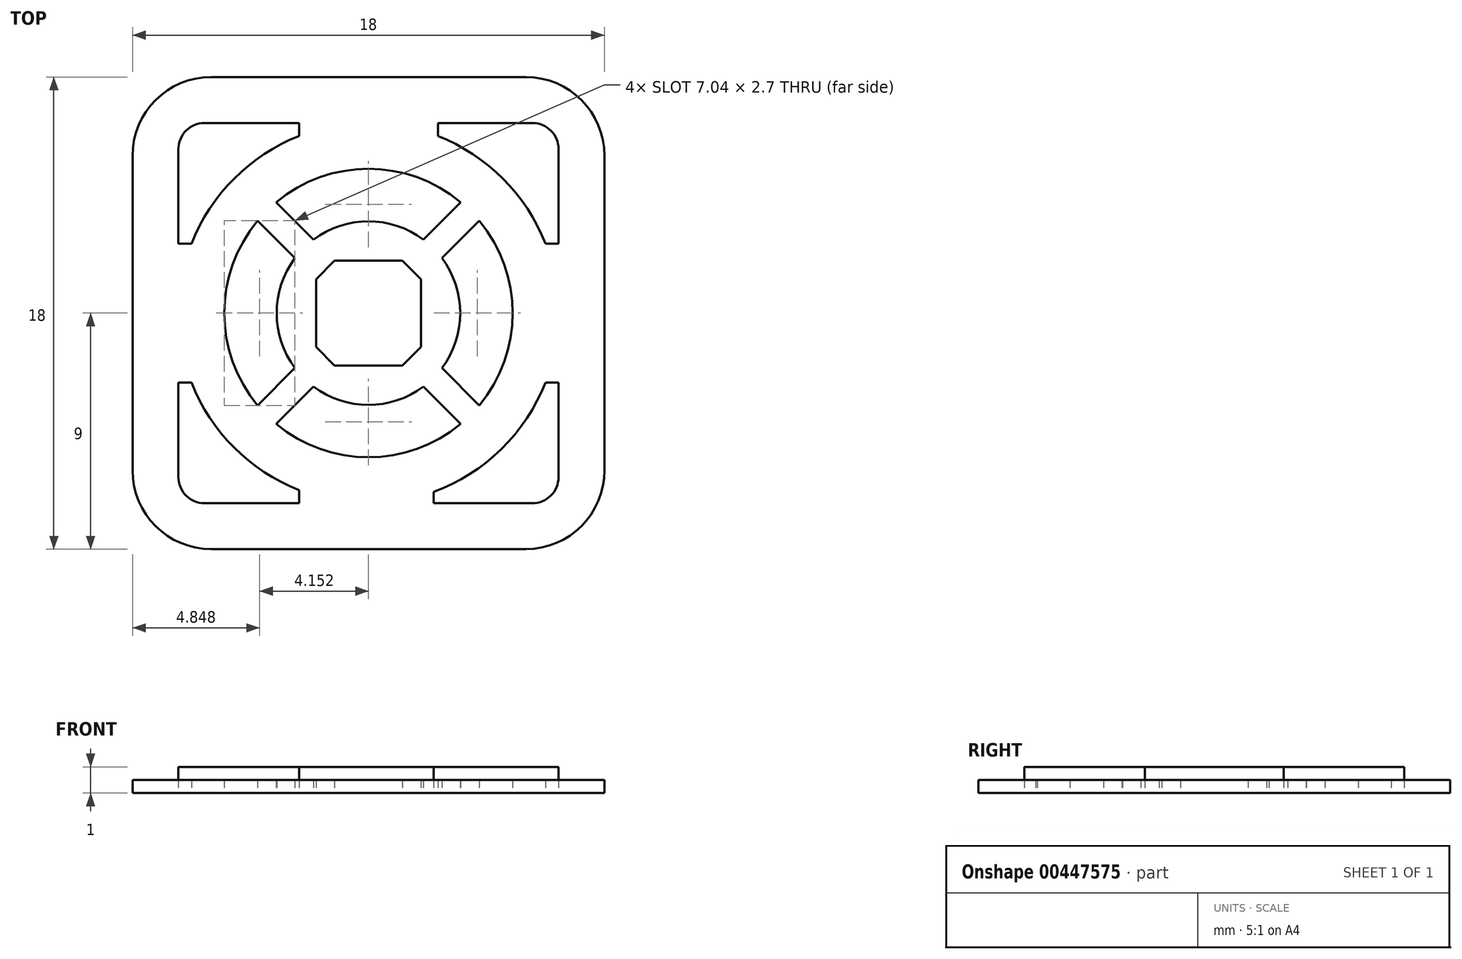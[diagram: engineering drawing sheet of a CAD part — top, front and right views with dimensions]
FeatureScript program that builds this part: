
annotation { "Feature Type Name" : "Feature", "Feature Type Description" : "" }
export const myFeature = defineFeature(function(context is Context, id is Id, definition is map)
    precondition{}
    {
        {
            var Q0;
            Q0=qCreatedBy(makeId("Top.planeOp"),FACE);
            var sketch = newSketch(context, id + "F0", { "sketchPlane" : qUnion([Q0])});
            skLineSegment(sketch, "E0.bottom", {"start": v(6, -9) * mm, "end": v(-6, -9) * mm});
            skLineSegment(sketch, "E0.top", {"start": v(6, 9) * mm, "end": v(-6, 9) * mm});
            skLineSegment(sketch, "E0.left", {"start": v(9, -6) * mm, "end": v(9, 6) * mm});
            skLineSegment(sketch, "E0.right", {"start": v(-9, -6) * mm, "end": v(-9, 6) * mm});
            skPoint(sketch, "E0.middle", {"position": v(0, 0) * mm});
            skLineSegment(sketch, "E1.bottom", {"start": v(1.3, -2) * mm, "end": v(-1.3, -2) * mm});
            skLineSegment(sketch, "E1.top", {"start": v(1.3, 2) * mm, "end": v(-1.3, 2) * mm});
            skLineSegment(sketch, "E1.left", {"start": v(2, -1.3) * mm, "end": v(2, 1.3) * mm});
            skLineSegment(sketch, "E1.right", {"start": v(-2, -1.3) * mm, "end": v(-2, 1.3) * mm});
            skLineSegment(sketch, "E2", {"start": v(-2, 1.3) * mm, "end": v(-1.3, 2) * mm});
            skLineSegment(sketch, "E3", {"start": v(1.3, 2) * mm, "end": v(2, 1.3) * mm});
            skLineSegment(sketch, "E4", {"start": v(-2, -1.3) * mm, "end": v(-1.3, -2) * mm});
            skLineSegment(sketch, "E5", {"start": v(1.3, -2) * mm, "end": v(2, -1.3) * mm});
            skPoint(sketch, "E6.orphan", {"position": v(-2, 2) * mm});
            skPoint(sketch, "E7.orphan", {"position": v(2, 2) * mm});
            skPoint(sketch, "E8.orphan", {"position": v(2, -2) * mm});
            skPoint(sketch, "E9.orphan", {"position": v(-2, -2) * mm});
            skArc(sketch, "E10", {"start": v(-2.8, 2.1) * mm, "mid": v(-3.5, 0) * mm, "end": v(-2.8, -2.1) * mm});
            skArc(sketch, "E11", {"start": v(-4.23, 3.52) * mm, "mid": v(-5.5, 0) * mm, "end": v(-4.23, -3.52) * mm});
            skLineSegment(sketch, "E12", {"start": v(-9, 9) * mm, "end": v(9, -9) * mm, "construction": true});
            skLineSegment(sketch, "E13", {"start": v(9, 9) * mm, "end": v(-9, -9) * mm, "construction": true});
            skLineSegment(sketch, "E14", {"start": v(-4.23, 3.52) * mm, "end": v(-2.8, 2.1) * mm});
            skLineSegment(sketch, "E15", {"start": v(-2.1, 2.8) * mm, "end": v(-3.52, 4.23) * mm});
            skLineSegment(sketch, "E16", {"start": v(2.1, 2.8) * mm, "end": v(3.52, 4.23) * mm});
            skLineSegment(sketch, "E17", {"start": v(2.8, 2.1) * mm, "end": v(4.23, 3.52) * mm});
            skLineSegment(sketch, "E18", {"start": v(-3.52, -4.23) * mm, "end": v(-2.1, -2.8) * mm});
            skLineSegment(sketch, "E19", {"start": v(-4.23, -3.52) * mm, "end": v(-2.8, -2.1) * mm});
            skLineSegment(sketch, "E20", {"start": v(2.1, -2.8) * mm, "end": v(3.52, -4.23) * mm});
            skLineSegment(sketch, "E21", {"start": v(2.8, -2.1) * mm, "end": v(4.23, -3.52) * mm});
            skArc(sketch, "E22.trimOffspring", {"start": v(-2.1, -2.8) * mm, "mid": v(0, -3.5) * mm, "end": v(2.1, -2.8) * mm});
            skArc(sketch, "E23.trimOffspring", {"start": v(-3.52, -4.23) * mm, "mid": v(0, -5.5) * mm, "end": v(3.52, -4.23) * mm});
            skArc(sketch, "E24.trimOffspring", {"start": v(2.8, -2.1) * mm, "mid": v(3.5, 0) * mm, "end": v(2.8, 2.1) * mm});
            skArc(sketch, "E25.trimOffspring", {"start": v(4.23, -3.52) * mm, "mid": v(5.5, 0) * mm, "end": v(4.23, 3.52) * mm});
            skArc(sketch, "E26.trimOffspring", {"start": v(2.1, 2.8) * mm, "mid": v(0, 3.5) * mm, "end": v(-2.1, 2.8) * mm});
            skArc(sketch, "E27.trimOffspring", {"start": v(3.52, 4.23) * mm, "mid": v(0, 5.5) * mm, "end": v(-3.52, 4.23) * mm});
            skArc(sketch, "E28", {"start": v(-6.75, -2.65) * mm, "mid": v(-5.13, -5.13) * mm, "end": v(-2.65, -6.75) * mm});
            skLineSegment(sketch, "E29.bottom", {"start": v(6.25, -7.25) * mm, "end": v(2.48, -7.25) * mm});
            skLineSegment(sketch, "E29.top", {"start": v(6.25, 7.25) * mm, "end": v(2.65, 7.25) * mm});
            skLineSegment(sketch, "E29.left", {"start": v(7.25, -6.25) * mm, "end": v(7.25, -2.65) * mm});
            skLineSegment(sketch, "E29.right", {"start": v(-7.25, -6.25) * mm, "end": v(-7.25, -2.65) * mm});
            skLineSegment(sketch, "E30", {"start": v(-2.65, 7.25) * mm, "end": v(-2.65, 6.75) * mm});
            skLineSegment(sketch, "E31", {"start": v(-7.25, 2.65) * mm, "end": v(-6.75, 2.65) * mm});
            skLineSegment(sketch, "E32", {"start": v(-7.25, -2.65) * mm, "end": v(-6.75, -2.65) * mm});
            skLineSegment(sketch, "E33", {"start": v(-2.65, -6.75) * mm, "end": v(-2.65, -7.25) * mm});
            skLineSegment(sketch, "E34", {"start": v(2.48, -6.75) * mm, "end": v(2.48, -7.25) * mm});
            skLineSegment(sketch, "E35", {"start": v(6.75, -2.65) * mm, "end": v(7.25, -2.65) * mm});
            skLineSegment(sketch, "E36", {"start": v(6.75, 2.65) * mm, "end": v(7.25, 2.65) * mm});
            skLineSegment(sketch, "E37", {"start": v(2.65, 6.75) * mm, "end": v(2.65, 7.25) * mm});
            skLineSegment(sketch, "E38.trimOffspring", {"start": v(-7.25, 2.65) * mm, "end": v(-7.25, 6.25) * mm});
            skArc(sketch, "E39.trimOffspring", {"start": v(2.48, -6.81) * mm, "mid": v(5.06, -5.19) * mm, "end": v(6.75, -2.65) * mm});
            skLineSegment(sketch, "E40.trimOffspring", {"start": v(-2.65, -7.25) * mm, "end": v(-6.25, -7.25) * mm});
            skArc(sketch, "E41.trimOffspring", {"start": v(6.75, 2.65) * mm, "mid": v(5.13, 5.13) * mm, "end": v(2.65, 6.75) * mm});
            skLineSegment(sketch, "E42.trimOffspring", {"start": v(7.25, 2.65) * mm, "end": v(7.25, 6.25) * mm});
            skLineSegment(sketch, "E43.trimOffspring", {"start": v(-2.65, 7.25) * mm, "end": v(-6.25, 7.25) * mm});
            skArc(sketch, "E44.trimOffspring", {"start": v(-2.65, 6.75) * mm, "mid": v(-5.13, 5.13) * mm, "end": v(-6.75, 2.65) * mm});
            skPoint(sketch, "E45.visualSharp", {"position": v(-7.25, 7.25) * mm});
            skArc(sketch, "E45.filletArc", {"start": v(-6.25, 7.25) * mm, "mid": v(-6.96, 6.96) * mm, "end": v(-7.25, 6.25) * mm});
            skPoint(sketch, "E46.visualSharp", {"position": v(7.25, 7.25) * mm});
            skArc(sketch, "E46.filletArc", {"start": v(7.25, 6.25) * mm, "mid": v(6.96, 6.96) * mm, "end": v(6.25, 7.25) * mm});
            skPoint(sketch, "E47.visualSharp", {"position": v(7.25, -7.25) * mm});
            skArc(sketch, "E47.filletArc", {"start": v(6.25, -7.25) * mm, "mid": v(6.96, -6.96) * mm, "end": v(7.25, -6.25) * mm});
            skPoint(sketch, "E48.visualSharp", {"position": v(-7.25, -7.25) * mm});
            skArc(sketch, "E48.filletArc", {"start": v(-7.25, -6.25) * mm, "mid": v(-6.96, -6.96) * mm, "end": v(-6.25, -7.25) * mm});
            skPoint(sketch, "E49.visualSharp", {"position": v(-9, 9) * mm});
            skArc(sketch, "E49.filletArc", {"start": v(-6, 9) * mm, "mid": v(-8.12, 8.12) * mm, "end": v(-9, 6) * mm});
            skPoint(sketch, "E50.visualSharp", {"position": v(9, 9) * mm});
            skArc(sketch, "E50.filletArc", {"start": v(9, 6) * mm, "mid": v(8.12, 8.12) * mm, "end": v(6, 9) * mm});
            skPoint(sketch, "E51.visualSharp", {"position": v(9, -9) * mm});
            skArc(sketch, "E51.filletArc", {"start": v(6, -9) * mm, "mid": v(8.12, -8.12) * mm, "end": v(9, -6) * mm});
            skPoint(sketch, "E52.visualSharp", {"position": v(-9, -9) * mm});
            skArc(sketch, "E52.filletArc", {"start": v(-9, -6) * mm, "mid": v(-8.12, -8.12) * mm, "end": v(-6, -9) * mm});
            skSolve(sketch);
        }
        {
            var Q0;
            Q0=makeQuery(id+"F0.imprint","IMPRINT",FACE,{"disambiguationData":[TD([[makeQuery(id+"F0.imprint","IMPRINT",EDGE,{"derivedFrom":sQuery(id+"F0.wireOp",EDGE,"E30")}),-1.0]])]});
            var Q1;
            Q1=makeQuery(id+"F0.imprint","IMPRINT",FACE,{"disambiguationData":[TD([[makeQuery(id+"F0.imprint","IMPRINT",EDGE,{"derivedFrom":sQuery(id+"F0.wireOp",EDGE,"E29.top")}),1.0]])]});
            var Q2;
            {var subQ1=sQuery(id+"F0.wireOp",EDGE,"E29.bottom");Q2=makeQuery(id+"F0.imprint","IMPRINT",FACE,{"disambiguationData":[TD([[makeQuery(id+"F0.imprint","IMPRINT",EDGE,{"derivedFrom":subQ1}),-1.0]])]});}
            var Q3;
            Q3=makeQuery(id+"F0.imprint","IMPRINT",FACE,{"disambiguationData":[TD([[makeQuery(id+"F0.imprint","IMPRINT",EDGE,{"derivedFrom":sQuery(id+"F0.wireOp",EDGE,"E28")}),-1.0]])]});
            var Q4;
            Q4=makeQuery(id+"F0.imprint","IMPRINT",FACE,{"disambiguationData":[TD([[makeQuery(id+"F0.imprint","IMPRINT",EDGE,{"derivedFrom":sQuery(id+"F0.wireOp",EDGE,"E10")}),-1.0]])]});
            var Q5;
            Q5=makeQuery(id+"F0.imprint","IMPRINT",FACE,{"disambiguationData":[TD([[makeQuery(id+"F0.imprint","IMPRINT",EDGE,{"derivedFrom":sQuery(id+"F0.wireOp",EDGE,"E15")}),-1.0]])]});
            var Q6;
            Q6=makeQuery(id+"F0.imprint","IMPRINT",FACE,{"disambiguationData":[TD([[makeQuery(id+"F0.imprint","IMPRINT",EDGE,{"derivedFrom":sQuery(id+"F0.wireOp",EDGE,"E17")}),-1.0]])]});
            var Q7;
            Q7=makeQuery(id+"F0.imprint","IMPRINT",FACE,{"disambiguationData":[TD([[makeQuery(id+"F0.imprint","IMPRINT",EDGE,{"derivedFrom":sQuery(id+"F0.wireOp",EDGE,"E18")}),-1.0]])]});
            var Q8;
            Q8=makeQuery(id+"F0.imprint","IMPRINT",FACE,{"disambiguationData":[TD([[makeQuery(id+"F0.imprint","IMPRINT",EDGE,{"derivedFrom":sQuery(id+"F0.wireOp",EDGE,"E1.bottom")}),-1.0]])]});
            extrude(context, id + "F1", {"entities" : qUnion([Q0, Q1, Q2, Q3, Q4, Q5, Q6, Q7, Q8]), "depth" : 1 * mm});
        }
        {
            var Q0;
            Q0=makeQuery(id+"F0.imprint","IMPRINT",FACE,{"disambiguationData":[TD([[makeQuery(id+"F0.imprint","IMPRINT",EDGE,{"derivedFrom":sQuery(id+"F0.wireOp",EDGE,"E0.bottom")}),-1.0]])]});
            extrude(context, id + "F2", {"entities" : qUnion([Q0]), "depth" : .5 * mm});
        }
    });
